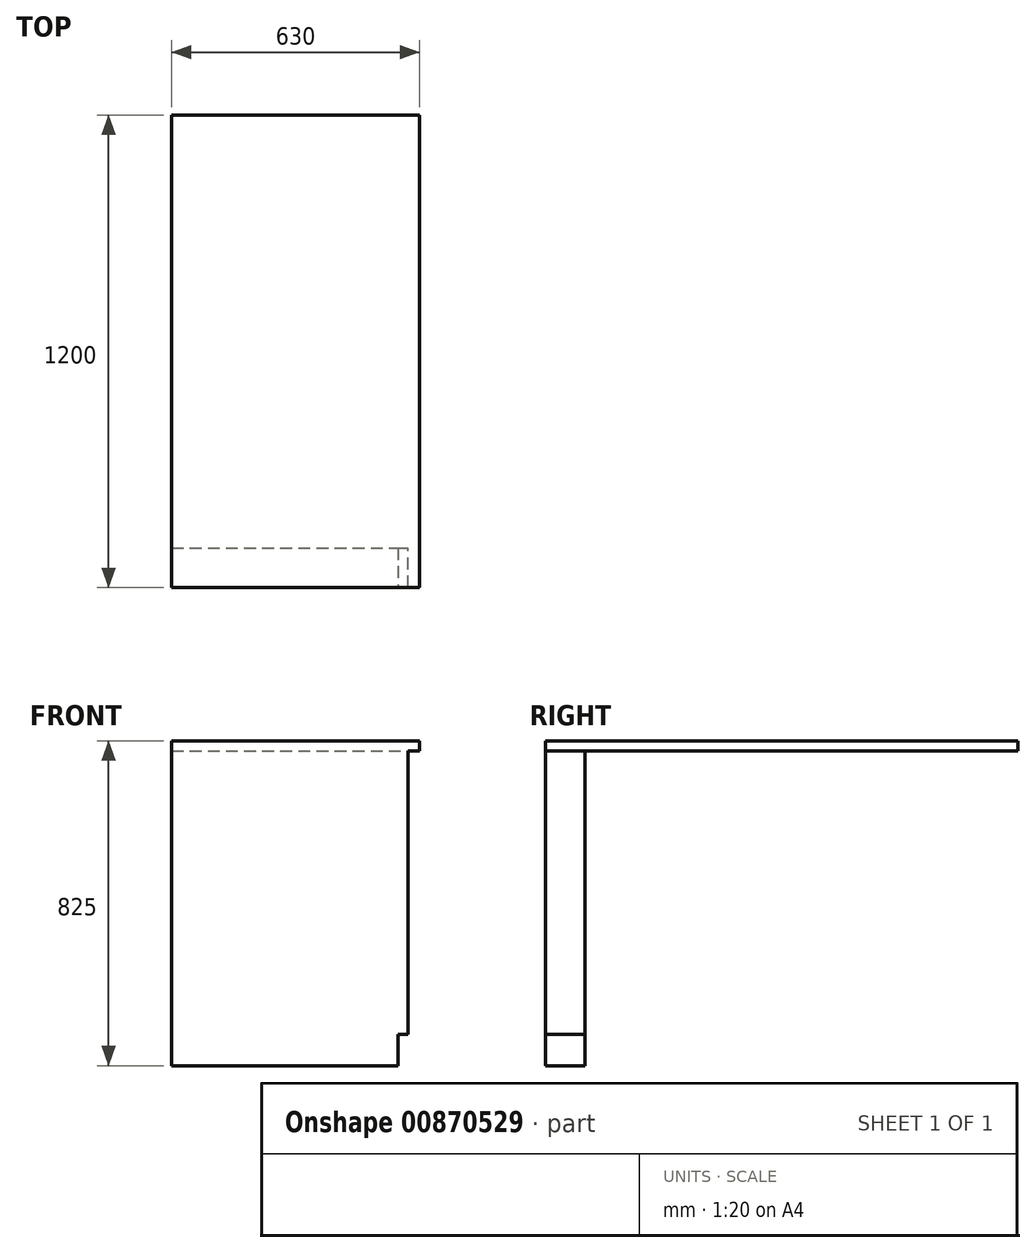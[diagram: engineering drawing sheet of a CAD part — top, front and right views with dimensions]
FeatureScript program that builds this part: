
annotation { "Feature Type Name" : "Feature", "Feature Type Description" : "" }
export const myFeature = defineFeature(function(context is Context, id is Id, definition is map)
    precondition{}
    {
        {
            var Q0;
            Q0=qCreatedBy(makeId("Top.planeOp"),FACE);
            var sketch = newSketch(context, id + "F0", { "sketchPlane" : qUnion([Q0])});
            skLineSegment(sketch, "E0.bottom", {"start": v(-300, 50) * mm, "end": v(300, 50) * mm});
            skLineSegment(sketch, "E0.top", {"start": v(-300, -50) * mm, "end": v(300, -50) * mm});
            skLineSegment(sketch, "E0.left", {"start": v(-300, 50) * mm, "end": v(-300, -50) * mm});
            skLineSegment(sketch, "E0.right", {"start": v(300, 50) * mm, "end": v(300, -50) * mm});
            skPoint(sketch, "E0.middle", {"position": v(0, 0) * mm});
            skSolve(sketch);
        }
        {
            var Q0;
            Q0=qSketchRegion(id+"F0",true);
            extrude(context, id + "F1", {"entities" : qUnion([Q0]), "depth" : 800 * mm, "offsetDistance" : 25 * mm});
        }
        {
            var Q0;
            Q0=makeQuery(id+"F1.opExtrude","SWEPT_FACE",FACE,{"disambiguationData":[OSD([sQuery(id+"F0.wireOp",EDGE,"E0.right")])]});
            var sketch = newSketch(context, id + "F2", { "sketchPlane" : qUnion([Q0])});
            skLineSegment(sketch, "E1.bottom", {"start": v(-50, 0) * mm, "end": v(50, 0) * mm});
            skLineSegment(sketch, "E1.top", {"start": v(-50, 80) * mm, "end": v(50, 80) * mm});
            skLineSegment(sketch, "E1.left", {"start": v(-50, 0) * mm, "end": v(-50, 80) * mm});
            skLineSegment(sketch, "E1.right", {"start": v(50, 0) * mm, "end": v(50, 80) * mm});
            skSolve(sketch);
        }
        {
            var Q0;
            Q0=qSketchRegion(id+"F2",true);
            extrude(context, id + "F3", {"entities" : qUnion([Q0]), "operationType" : NewBodyOperationType.REMOVE, "oppositeDirection" : true, "depth" : 25 * mm, "offsetDistance" : 25 * mm});
        }
        {
            var Q0;
            Q0=makeQuery(id+"F1.opExtrude","CAP_FACE",FACE,{"disambiguationData":[OSD([sQuery(id+"F0.wireOp",EDGE,"E0.bottom"),sQuery(id+"F0.wireOp",EDGE,"E0.top"),sQuery(id+"F0.wireOp",EDGE,"E0.left"),sQuery(id+"F0.wireOp",EDGE,"E0.right")])],"isStart":false});
            var sketch = newSketch(context, id + "F4", { "sketchPlane" : qUnion([Q0])});
            skLineSegment(sketch, "E2.bottom", {"start": v(-300, -50) * mm, "end": v(330, -50) * mm});
            skLineSegment(sketch, "E2.top", {"start": v(-300, 50) * mm, "end": v(330, 50) * mm});
            skLineSegment(sketch, "E2.left", {"start": v(-300, -50) * mm, "end": v(-300, 50) * mm});
            skLineSegment(sketch, "E2.right", {"start": v(330, -50) * mm, "end": v(330, 50) * mm});
            skSolve(sketch);
        }
        {
            var Q0;
            Q0=qSketchRegion(id+"F4",true);
            extrude(context, id + "F5", {"entities" : qUnion([Q0]), "operationType" : NewBodyOperationType.ADD, "depth" : 25 * mm, "offsetDistance" : 25 * mm});
        }
        {
            var Q0;
            Q0=makeQuery(id+"F5.boolean.opBoolean","MERGE",FACE,{"derivedFrom":[makeQuery(id+"F1.opExtrude","SWEPT_FACE",FACE,{"disambiguationData":[OSD([sQuery(id+"F0.wireOp",EDGE,"E0.bottom")])]}),makeQuery(id+"F5.opExtrude","SWEPT_FACE",FACE,{"disambiguationData":[OSD([sQuery(id+"F4.wireOp",EDGE,"E2.top")])]})]});
            var sketch = newSketch(context, id + "F6", { "sketchPlane" : qUnion([Q0])});
            skLineSegment(sketch, "E3.bottom", {"start": v(-330, 800) * mm, "end": v(300, 800) * mm});
            skLineSegment(sketch, "E3.top", {"start": v(-330, 825) * mm, "end": v(300, 825) * mm});
            skLineSegment(sketch, "E3.left", {"start": v(-330, 800) * mm, "end": v(-330, 825) * mm});
            skLineSegment(sketch, "E3.right", {"start": v(300, 800) * mm, "end": v(300, 825) * mm});
            skSolve(sketch);
        }
        {
            var Q0;
            Q0 = qSketchRegion(id + "F6", true);
            extrude(context, id + "F7", {"entities" : qUnion([Q0]), "operationType" : NewBodyOperationType.ADD, "depth" : 1100 * mm, "offsetDistance" : 25 * mm});
        }
    });
